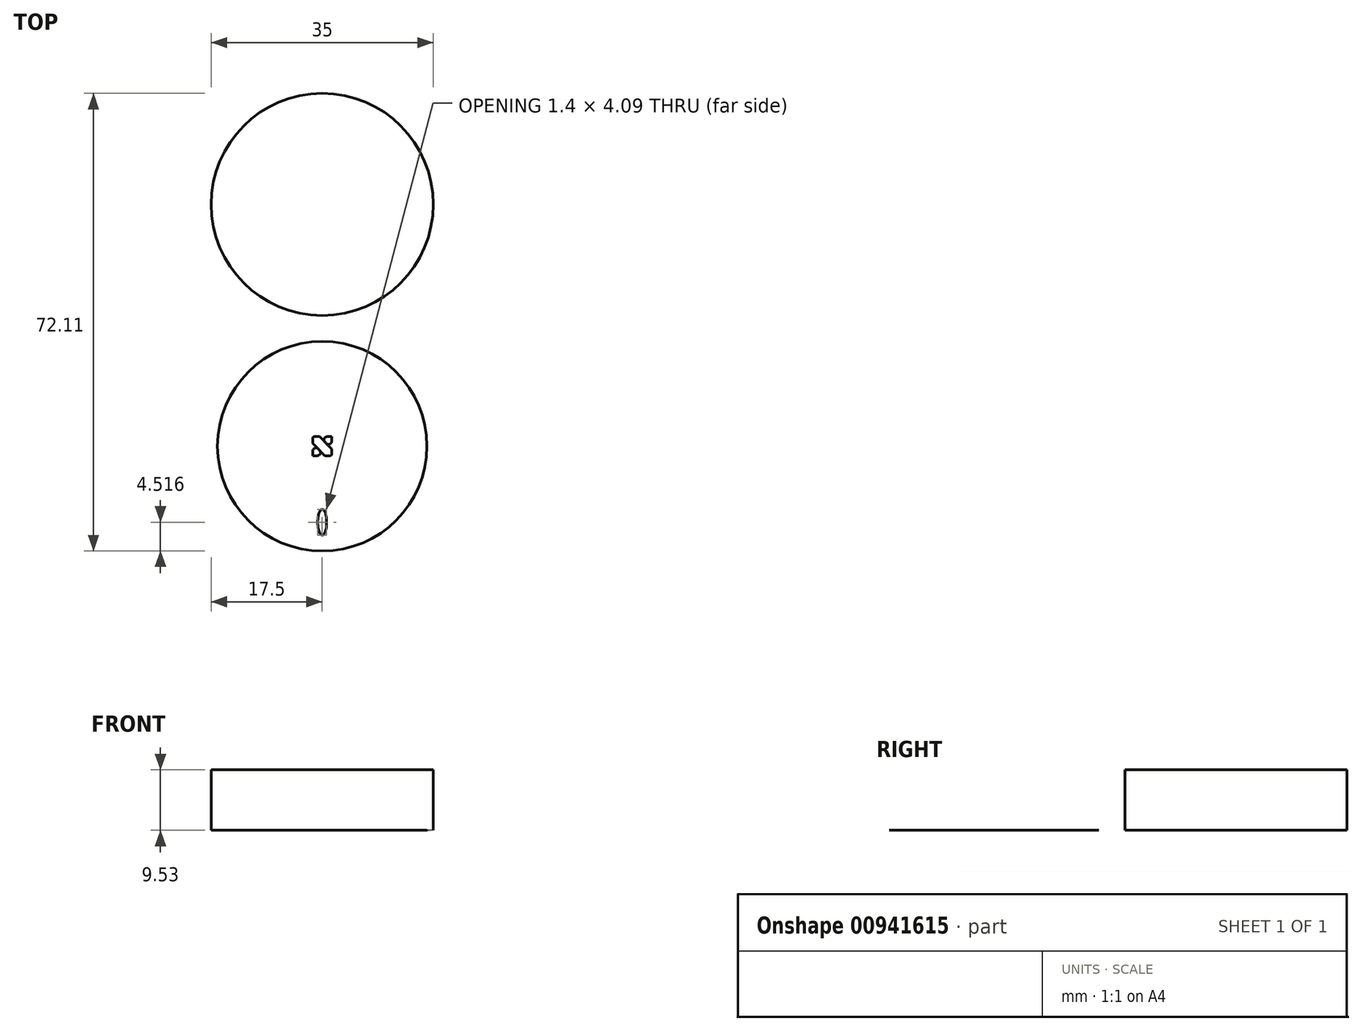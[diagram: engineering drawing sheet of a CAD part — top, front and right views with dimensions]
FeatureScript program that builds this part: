
annotation { "Feature Type Name" : "Feature", "Feature Type Description" : "" }
export const myFeature = defineFeature(function(context is Context, id is Id, definition is map)
    precondition{}
    {
        {
            var Q0;
            Q0=qCreatedBy(makeId("Top.planeOp"),FACE);
            var sketch = newSketch(context, id + "F0", { "sketchPlane" : qUnion([Q0])});
            skCircle(sketch, "E0", {"center": v(0, 0) * mm, "radius": 16.51 * mm});
            skSolve(sketch);
        }
        {
            var Q0;
            Q0=makeQuery(id+"F0.imprint","IMPRINT",FACE,{"disambiguationData":[TD([[makeQuery(id+"F0.imprint","IMPRINT",EDGE,{"derivedFrom":sQuery(id+"F0.wireOp",EDGE,"E0")}),1.0]])]});
            extrude(context, id + "F1", {"entities" : qUnion([Q0]), "depth" : 1 / 406.4 * mm, "offsetDistance" : 25.4 * mm});
        }
        {
            var Q0;
            Q0=makeQuery(id+"F1.opExtrude","CAP_FACE",FACE,{"disambiguationData":[OSD([sQuery(id+"F0.wireOp",EDGE,"E0")])],"isStart":false});
            var sketch = newSketch(context, id + "F2", { "sketchPlane" : qUnion([Q0])});
            skLineSegment(sketch, "E1.bottom", {"start": v(1.5, -1.5) * mm, "end": v(-1.5, -1.5) * mm});
            skLineSegment(sketch, "E1.top", {"start": v(1.5, 1.5) * mm, "end": v(-1.5, 1.5) * mm});
            skLineSegment(sketch, "E1.left", {"start": v(1.5, -1.5) * mm, "end": v(1.5, 1.5) * mm});
            skLineSegment(sketch, "E1.right", {"start": v(-1.5, -1.5) * mm, "end": v(-1.5, 1.5) * mm});
            skPoint(sketch, "E1.middle", {"position": v(0, 0) * mm});
            skSolve(sketch);
        }
        {
            var Q0;
            Q0=makeQuery(id+"F2.imprint","IMPRINT",FACE,{"disambiguationData":[TD([[makeQuery(id+"F2.imprint","IMPRINT",EDGE,{"derivedFrom":sQuery(id+"F2.wireOp",EDGE,"E1.bottom")}),-1.0]])]});
            extrude(context, id + "F3", {"entities" : qUnion([Q0]), "operationType" : NewBodyOperationType.ADD, "depth" : 2 / 406.4 * mm, "offsetDistance" : 25.4 * mm});
        }
        {
            var Q0;
            Q0=makeQuery(id+"F3.opExtrude","SWEPT_FACE",FACE,{"disambiguationData":[OSD([sQuery(id+"F2.wireOp",EDGE,"E1.bottom")])]});
            var sketch = newSketch(context, id + "F4", { "sketchPlane" : qUnion([Q0])});
            skCircle(sketch, "E2", {"center": v(0, 3.76) * mm, "radius": 0.7 * mm});
            skSolve(sketch);
        }
        {
            var Q0;
            Q0=makeQuery(id+"F3.opExtrude","SWEPT_FACE",FACE,{"disambiguationData":[OSD([sQuery(id+"F2.wireOp",EDGE,"E1.left")])]});
            var sketch = newSketch(context, id + "F5", { "sketchPlane" : qUnion([Q0])});
            skCircle(sketch, "E3", {"center": v(0, 3.76) * mm, "radius": 0.7 * mm});
            skSolve(sketch);
        }
        {
            var Q0;
            Q0=makeQuery(id+"F3.opExtrude","SWEPT_FACE",FACE,{"disambiguationData":[OSD([sQuery(id+"F2.wireOp",EDGE,"E1.right")])]});
            var sketch = newSketch(context, id + "F6", { "sketchPlane" : qUnion([Q0])});
            skCircle(sketch, "E4", {"center": v(0, 3.76) * mm, "radius": 0.7 * mm});
            skSolve(sketch);
        }
        {
            var Q0;
            Q0=makeQuery(id+"F3.opExtrude","SWEPT_FACE",FACE,{"disambiguationData":[OSD([sQuery(id+"F2.wireOp",EDGE,"E1.top")])]});
            var sketch = newSketch(context, id + "F7", { "sketchPlane" : qUnion([Q0])});
            skCircle(sketch, "E5", {"center": v(0, 3.76) * mm, "radius": 0.7 * mm});
            skPoint(sketch, "E6", {"position": v(-0.7, 3.76) * mm});
            skSolve(sketch);
        }
        {
            var Q0;
            Q0=makeQuery(id+"F3.opExtrude","CAP_FACE",FACE,{"disambiguationData":[OSD([sQuery(id+"F2.wireOp",EDGE,"E1.bottom"),sQuery(id+"F2.wireOp",EDGE,"E1.top"),sQuery(id+"F2.wireOp",EDGE,"E1.left"),sQuery(id+"F2.wireOp",EDGE,"E1.right")])],"isStart":false});
            var sketch = newSketch(context, id + "F8", { "sketchPlane" : qUnion([Q0])});
            skLineSegment(sketch, "E7.bottom", {"start": v(0.53, -1.6) * mm, "end": v(-1.6, 0.53) * mm});
            skLineSegment(sketch, "E7.top", {"start": v(1.6, -0.53) * mm, "end": v(-0.53, 1.6) * mm});
            skLineSegment(sketch, "E7.left", {"start": v(0.53, -1.6) * mm, "end": v(1.6, -0.53) * mm});
            skLineSegment(sketch, "E7.right", {"start": v(-1.6, 0.53) * mm, "end": v(-0.53, 1.6) * mm});
            skPoint(sketch, "E7.middle", {"position": v(0, 0) * mm});
            skSolve(sketch);
        }
        {
            var Q0;
            {var subQ0=sQuery(id+"F8.wireOp",EDGE,"E7.top");var subQ1=makeQuery(id+"F3.opExtrude","CAP_EDGE",EDGE,{"disambiguationData":[OSD([sQuery(id+"F2.wireOp",EDGE,"E1.left")])],"isStart":false});var subQ2=makeQuery(id+"F8.imprint","INTERSECT",VERTEX,{"derivedFrom":[subQ1,subQ0]});Q0=makeQuery(id+"F8.imprint","IMPRINT",FACE,{"disambiguationData":[TD([[makeQuery(id+"F8.imprint","IMPRINT",EDGE,{"disambiguationData":[TD([[subQ2,-1.0]])],"derivedFrom":subQ0}),-1.0]])]});}
            var Q1;
            {var subQ0=sQuery(id+"F8.wireOp",EDGE,"E7.bottom");var subQ1=makeQuery(id+"F3.opExtrude","CAP_EDGE",EDGE,{"disambiguationData":[OSD([sQuery(id+"F2.wireOp",EDGE,"E1.bottom")])],"isStart":false});var subQ2=makeQuery(id+"F8.imprint","INTERSECT",VERTEX,{"derivedFrom":[subQ1,subQ0]});Q1=makeQuery(id+"F8.imprint","IMPRINT",FACE,{"disambiguationData":[TD([[makeQuery(id+"F8.imprint","IMPRINT",EDGE,{"disambiguationData":[TD([[subQ2,-1.0]])],"derivedFrom":subQ0}),1.0]])]});}
            extrude(context, id + "F9", {"entities" : qUnion([Q0, Q1]), "operationType" : NewBodyOperationType.REMOVE, "oppositeDirection" : true, "depth" : 2.5 * mm, "offsetDistance" : 25.4 * mm});
        }
        {
            var Q0;
            Q0=qCreatedBy(makeId("Top.planeOp"),FACE);
            var sketch = newSketch(context, id + "F10", { "sketchPlane" : qUnion([Q0])});
            skCircle(sketch, "E8", {"center": v(0, 38.1) * mm, "radius": 17.5 * mm});
            skSolve(sketch);
        }
        {
            var Q0;
            Q0=makeQuery(id+"F10.imprint","IMPRINT",FACE,{"disambiguationData":[TD([[makeQuery(id+"F10.imprint","IMPRINT",EDGE,{"derivedFrom":sQuery(id+"F10.wireOp",EDGE,"E8")}),1.0]])]});
            extrude(context, id + "F11", {"entities" : qUnion([Q0]), "operationType" : NewBodyOperationType.ADD, "depth" : 9.52 * mm, "offsetDistance" : 25.4 * mm});
        }
        {
            var Q0;
            Q0=makeQuery(id+"F1.opExtrude","SWEPT_BODY",BODY,{"disambiguationData":[OSD([sQuery(id+"F0.wireOp",EDGE,"E0")])]});
            var Q1;
            Q1=makeQuery(id+"F11.opExtrude","SWEPT_BODY",BODY,{"disambiguationData":[OSD([sQuery(id+"F10.wireOp",EDGE,"E8")])]});
            booleanBodies(context, id + "F12", {"operationType" : BooleanOperationType.SUBTRACTION, "tools" : qUnion([Q0]), "targets" : qUnion([Q1]), "keepTools" : true});
        }
        {
            var Q0;
            Q0=makeQuery(id+"F3.opExtrude","SWEPT_FACE",FACE,{"disambiguationData":[OSD([sQuery(id+"F2.wireOp",EDGE,"E1.bottom")])]});
            var sketch = newSketch(context, id + "F13", { "sketchPlane" : qUnion([Q0])});
            skLineSegment(sketch, "E9", {"start": v(-1, 3.18) * mm, "end": v(1, 3.18) * mm});
            skSolve(sketch);
        }
        {
            var Q0;
            Q0=sQuery(id+"F13.wireOp",EDGE,"E9");
            cPlane(context, id + "F14", {"entities" : qUnion([Q0]), "cplaneType" : CPlaneType.LINE_ANGLE, "offset" : 25.4 * mm, "angle" : 20 * degree, "width" : 152.4 * mm, "height" : 152.4 * mm});
        }
        {
            var Q0;
            Q0=qCreatedBy(id+"F14.planeOp",FACE);
            cPlane(context, id + "F15", {"entities" : qUnion([Q0]), "cplaneType" : CPlaneType.OFFSET, "offset" : 0.5 * mm, "oppositeDirection" : true, "width" : 152.4 * mm, "height" : 152.4 * mm});
        }
        {
            var Q0;
            Q0=qCreatedBy(id+"F15.planeOp",FACE);
            var sketch = newSketch(context, id + "F16", { "sketchPlane" : qUnion([Q0])});
            skCircle(sketch, "E10", {"center": v(0, 4.1) * mm, "radius": 0.7 * mm});
            skSolve(sketch);
        }
        {
            var Q0;
            Q0=makeQuery(id+"F16.imprint","IMPRINT",FACE,{"disambiguationData":[TD([[makeQuery(id+"F16.imprint","IMPRINT",EDGE,{"derivedFrom":sQuery(id+"F16.wireOp",EDGE,"E10")}),1.0]])]});
            extrude(context, id + "F17", {"entities" : qUnion([Q0]), "operationType" : NewBodyOperationType.REMOVE, "depth" : 1.27 * mm, "offsetDistance" : 25.4 * mm});
        }
        {
            var Q0;
            Q0 = qSketchRegion(id + "F16", true);
            extrude(context, id + "F18", {"entities" : qUnion([Q0]), "operationType" : NewBodyOperationType.REMOVE, "oppositeDirection" : true, "depth" : 25.4 * mm, "offsetDistance" : 25.4 * mm});
        }
        {
            var Q0;
            Q0=makeQuery(id+"F3.opExtrude","SWEPT_EDGE",EDGE,{"disambiguationData":[OSD([sQuery(id+"F2.wireOp",EDGE,"E1.bottom"),sQuery(id+"F2.wireOp",EDGE,"E1.left")])]});
            var Q1;
            Q1=makeQuery(id+"F3.opExtrude","SWEPT_EDGE",EDGE,{"disambiguationData":[OSD([sQuery(id+"F2.wireOp",EDGE,"E1.top"),sQuery(id+"F2.wireOp",EDGE,"E1.right")])]});
            var Q2;
            Q2=makeQuery(id+"F3.opExtrude","SWEPT_EDGE",EDGE,{"disambiguationData":[OSD([sQuery(id+"F2.wireOp",EDGE,"E1.top"),sQuery(id+"F2.wireOp",EDGE,"E1.left")])]});
            var Q3;
            Q3=makeQuery(id+"F3.opExtrude","SWEPT_EDGE",EDGE,{"disambiguationData":[OSD([sQuery(id+"F2.wireOp",EDGE,"E1.bottom"),sQuery(id+"F2.wireOp",EDGE,"E1.right")])]});
            fillet(context, id + "F19", {"entities" : qUnion([Q0, Q1, Q2, Q3]), "radius" : 0.25 * mm, "tangentPropagation" : true, "allowEdgeOverflow" : false});
        }
        {
            var Q0;
            {var subQ0=sQuery(id+"F2.wireOp",EDGE,"E1.left");var subQ1=sQuery(id+"F8.wireOp",EDGE,"E7.top");Q0=makeQuery(id+"FtQDKmiVRhpXAqY_2.3.F17.boolean.opBoolean","SPLIT",EDGE,{"disambiguationData":[TD([makeQuery(id+"F9.boolean.opBoolean","COPY",FACE,{"derivedFrom":makeQuery(id+"F9.opExtrude","CAP_FACE",FACE,{"disambiguationData":[OSD([sQuery(id+"F2.wireOp",EDGE,"E1.top"),subQ0,subQ1])],"isStart":false})})])],"derivedFrom":makeQuery(id+"F9.boolean.opBoolean","COPY",EDGE,{"derivedFrom":makeQuery(id+"F9.opExtrude","SWEPT_EDGE",EDGE,{"disambiguationData":[OSD([subQ0,subQ1])]})})});}
            var Q1;
            {var subQ0=sQuery(id+"F2.wireOp",EDGE,"E1.top");var subQ1=sQuery(id+"F8.wireOp",EDGE,"E7.top");Q1=makeQuery(id+"FtQDKmiVRhpXAqY_2.2.F17.boolean.opBoolean","SPLIT",EDGE,{"disambiguationData":[TD([makeQuery(id+"F9.boolean.opBoolean","COPY",FACE,{"derivedFrom":makeQuery(id+"F9.opExtrude","CAP_FACE",FACE,{"disambiguationData":[OSD([subQ0,sQuery(id+"F2.wireOp",EDGE,"E1.left"),subQ1])],"isStart":false})})])],"derivedFrom":makeQuery(id+"F9.boolean.opBoolean","COPY",EDGE,{"derivedFrom":makeQuery(id+"F9.opExtrude","SWEPT_EDGE",EDGE,{"disambiguationData":[OSD([subQ0,subQ1])]})})});}
            var Q2;
            {var subQ0=sQuery(id+"F2.wireOp",EDGE,"E1.right");var subQ1=sQuery(id+"F8.wireOp",EDGE,"E7.bottom");Q2=makeQuery(id+"FtQDKmiVRhpXAqY_2.1.F17.boolean.opBoolean","SPLIT",EDGE,{"disambiguationData":[TD([makeQuery(id+"F9.boolean.opBoolean","COPY",FACE,{"derivedFrom":makeQuery(id+"F9.opExtrude","CAP_FACE",FACE,{"disambiguationData":[OSD([sQuery(id+"F2.wireOp",EDGE,"E1.bottom"),subQ0,subQ1])],"isStart":false})})])],"derivedFrom":makeQuery(id+"F9.boolean.opBoolean","COPY",EDGE,{"derivedFrom":makeQuery(id+"F9.opExtrude","SWEPT_EDGE",EDGE,{"disambiguationData":[OSD([subQ0,subQ1])]})})});}
            var Q3;
            {var subQ0=sQuery(id+"F2.wireOp",EDGE,"E1.bottom");var subQ1=sQuery(id+"F8.wireOp",EDGE,"E7.bottom");Q3=makeQuery(id+"F17.boolean.opBoolean","SPLIT",EDGE,{"disambiguationData":[TD([makeQuery(id+"F9.boolean.opBoolean","COPY",FACE,{"derivedFrom":makeQuery(id+"F9.opExtrude","CAP_FACE",FACE,{"disambiguationData":[OSD([subQ0,sQuery(id+"F2.wireOp",EDGE,"E1.right"),subQ1])],"isStart":false})})])],"derivedFrom":makeQuery(id+"F9.boolean.opBoolean","COPY",EDGE,{"derivedFrom":makeQuery(id+"F9.opExtrude","SWEPT_EDGE",EDGE,{"disambiguationData":[OSD([subQ0,subQ1])]})})});}
            var Q4;
            {var subQ0=sQuery(id+"F2.wireOp",EDGE,"E1.left");var subQ1=sQuery(id+"F8.wireOp",EDGE,"E7.top");Q4=makeQuery(id+"FtQDKmiVRhpXAqY_2.3.F17.boolean.opBoolean","SPLIT",EDGE,{"disambiguationData":[TD([makeQuery(id+"F3.opExtrude","CAP_FACE",FACE,{"disambiguationData":[OSD([sQuery(id+"F2.wireOp",EDGE,"E1.bottom"),sQuery(id+"F2.wireOp",EDGE,"E1.top"),subQ0,sQuery(id+"F2.wireOp",EDGE,"E1.right")])],"isStart":false})])],"derivedFrom":makeQuery(id+"F9.boolean.opBoolean","COPY",EDGE,{"derivedFrom":makeQuery(id+"F9.opExtrude","SWEPT_EDGE",EDGE,{"disambiguationData":[OSD([subQ0,subQ1])]})})});}
            var Q5;
            {var subQ0=sQuery(id+"F2.wireOp",EDGE,"E1.top");var subQ1=sQuery(id+"F8.wireOp",EDGE,"E7.top");Q5=makeQuery(id+"FtQDKmiVRhpXAqY_2.2.F17.boolean.opBoolean","SPLIT",EDGE,{"disambiguationData":[TD([makeQuery(id+"F3.opExtrude","CAP_FACE",FACE,{"disambiguationData":[OSD([sQuery(id+"F2.wireOp",EDGE,"E1.bottom"),subQ0,sQuery(id+"F2.wireOp",EDGE,"E1.left"),sQuery(id+"F2.wireOp",EDGE,"E1.right")])],"isStart":false})])],"derivedFrom":makeQuery(id+"F9.boolean.opBoolean","COPY",EDGE,{"derivedFrom":makeQuery(id+"F9.opExtrude","SWEPT_EDGE",EDGE,{"disambiguationData":[OSD([subQ0,subQ1])]})})});}
            var Q6;
            {var subQ0=sQuery(id+"F2.wireOp",EDGE,"E1.bottom");var subQ1=sQuery(id+"F8.wireOp",EDGE,"E7.bottom");Q6=makeQuery(id+"F17.boolean.opBoolean","SPLIT",EDGE,{"disambiguationData":[TD([makeQuery(id+"F3.opExtrude","CAP_FACE",FACE,{"disambiguationData":[OSD([subQ0,sQuery(id+"F2.wireOp",EDGE,"E1.top"),sQuery(id+"F2.wireOp",EDGE,"E1.left"),sQuery(id+"F2.wireOp",EDGE,"E1.right")])],"isStart":false})])],"derivedFrom":makeQuery(id+"F9.boolean.opBoolean","COPY",EDGE,{"derivedFrom":makeQuery(id+"F9.opExtrude","SWEPT_EDGE",EDGE,{"disambiguationData":[OSD([subQ0,subQ1])]})})});}
            var Q7;
            {var subQ0=sQuery(id+"F2.wireOp",EDGE,"E1.right");var subQ1=sQuery(id+"F8.wireOp",EDGE,"E7.bottom");Q7=makeQuery(id+"FtQDKmiVRhpXAqY_2.1.F17.boolean.opBoolean","SPLIT",EDGE,{"disambiguationData":[TD([makeQuery(id+"F3.opExtrude","CAP_FACE",FACE,{"disambiguationData":[OSD([sQuery(id+"F2.wireOp",EDGE,"E1.bottom"),sQuery(id+"F2.wireOp",EDGE,"E1.top"),sQuery(id+"F2.wireOp",EDGE,"E1.left"),subQ0])],"isStart":false})])],"derivedFrom":makeQuery(id+"F9.boolean.opBoolean","COPY",EDGE,{"derivedFrom":makeQuery(id+"F9.opExtrude","SWEPT_EDGE",EDGE,{"disambiguationData":[OSD([subQ0,subQ1])]})})});}
            fillet(context, id + "F20", {"entities" : qUnion([Q0, Q1, Q2, Q3, Q4, Q5, Q6, Q7]), "radius" : 0.5 * mm, "tangentPropagation" : true, "allowEdgeOverflow" : false});
        }
    });
